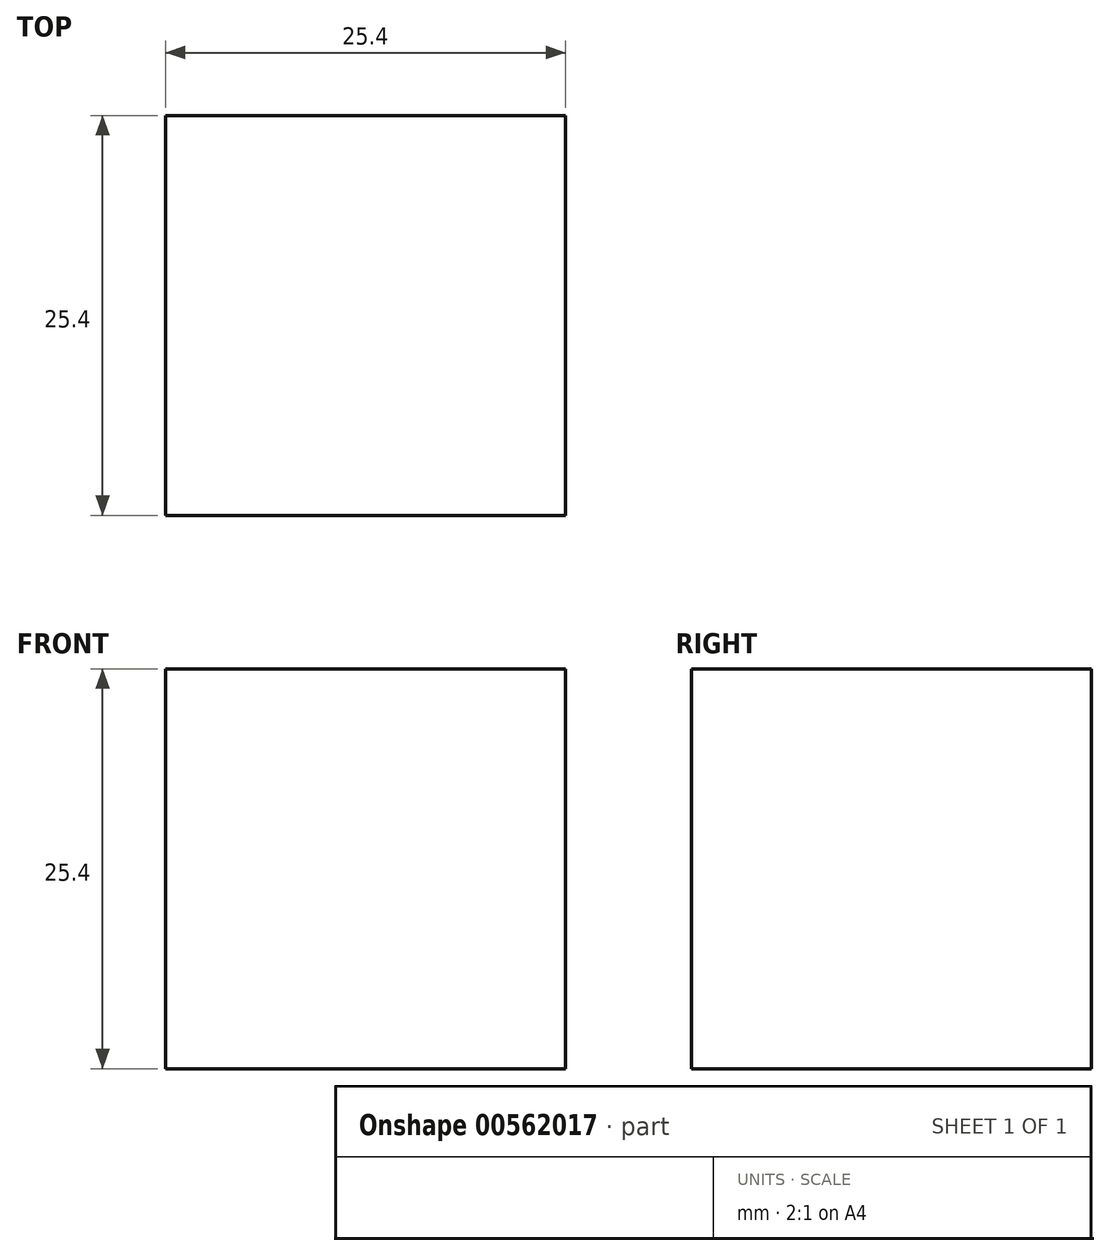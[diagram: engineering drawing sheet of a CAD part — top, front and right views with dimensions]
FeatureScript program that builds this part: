
annotation { "Feature Type Name" : "Feature", "Feature Type Description" : "" }
export const myFeature = defineFeature(function(context is Context, id is Id, definition is map)
    precondition{}
    {
        {
            var Q0;
            Q0=qCreatedBy(makeId("Front.planeOp"),FACE);
            var sketch = newSketch(context, id + "F0", { "sketchPlane" : qUnion([Q0])});
            skLineSegment(sketch, "E0.bottom", {"start": v(-69.5, 43.67) * mm, "end": v(-44.1, 43.67) * mm});
            skLineSegment(sketch, "E0.top", {"start": v(-69.5, 18.27) * mm, "end": v(-44.1, 18.27) * mm});
            skLineSegment(sketch, "E0.left", {"start": v(-69.5, 43.67) * mm, "end": v(-69.5, 18.27) * mm});
            skLineSegment(sketch, "E0.right", {"start": v(-44.1, 43.67) * mm, "end": v(-44.1, 18.27) * mm});
            skSolve(sketch);
        }
        {
            var Q0;
            Q0 = qSketchRegion(id + "F0", true);
            extrude(context, id + "F1", {"entities" : qUnion([Q0]), "depth" : 25.4 * mm, "offsetDistance" : 25.4 * mm});
        }
    });
